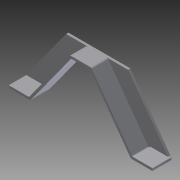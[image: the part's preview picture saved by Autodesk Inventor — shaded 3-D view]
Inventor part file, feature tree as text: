
AUTODESK INVENTOR PART (.ipt)
format: ipt  version: 2012 (Build 160160000, 160)  size: 121,856 bytes
history: native  units: in
note: dims shown in document units (in); Inventor stores cm internally (conversion verified against a paired STEP export)
features: extrude x2, fillet x2, sketch x1
ambient origin geometry x8: Origin, YZ Plane, XZ Plane, XY Plane, X Axis, Y Axis, Z Axis, Center Point
bodies: Solid1 (feature_tree)
feature tree (5):
  sketch  "Sketch1"  dims[d0=7.625in d1=1.0in d2=1.0in d3=1.0in d4=0.125in d5=0.125in d6=3.0in d7=0.0625in d8=0.0625in d9=0.0625in d10=1.0in d11=0.0in d12=0.125in d13=0.0in d14=0.0625in d15=0.125in]
  extrude  "Extrusion1"  Depth=1.0in
  extrude  "Extrusion2"  Depth=1.0in
  fillet  "Fillet1"  Radius=1.0in
  fillet  "Fillet2"  Radius=0.125in
